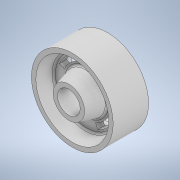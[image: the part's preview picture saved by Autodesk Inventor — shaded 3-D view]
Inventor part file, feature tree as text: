
AUTODESK INVENTOR PART (.ipt)
format: ipt  version: 2021 (Build 250183000, 183)  size: 225,280 bytes
history: native  units: mm
features: sketch x2, revolve x1, plane x1, extrude x1
ambient origin geometry x8: Origin, YZ Plane, XZ Plane, XY Plane, X Axis, Y Axis, Z Axis, Center Point
bodies: Solid1 (feature_tree)
feature tree (5):
  sketch  "Sketch1"  dims[d0=43.0mm d1=4.5mm]
  revolve  "Revolution1"  [1 undecoded]
  plane  "Work Plane1"
  extrude  "Extrusion1"  Depth=21.5mm
  sketch  "Sketch2"  dims[d2=15.0deg d3=21.5mm d4=3.5mm d5=4.5mm d6=36.0mm d7=18.0mm d8=15.0deg d9=3.5mm d10=30.0mm d11=2.0mm d12=32.0mm d13=90.0deg d14=50.0mm d15=29.410882mm d16=22.5deg d17=22.5deg d20=0.0mm d21=0.0mm]
note: 1 required parameter value undecoded (feature->parameter linkage not recoverable at this tier; creation-order binding heuristic only, values carry confidence <= 0.55)
